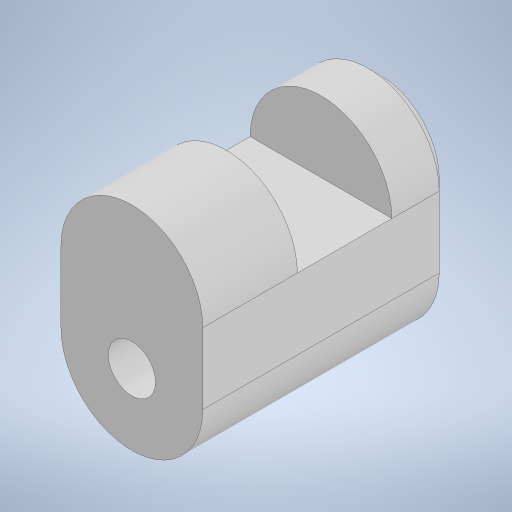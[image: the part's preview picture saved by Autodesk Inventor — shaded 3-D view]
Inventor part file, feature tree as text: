
AUTODESK INVENTOR PART (.ipt)
format: ipt  version: 2024.1 (Build 281209000, 209)  size: 236,544 bytes
history: native  units: mm
features: extrude x4, sketch x4, projected_geometry x3, chamfer x2
ambient origin geometry x8: Origin, YZ Plane, XZ Plane, XY Plane, X Axis, Y Axis, Z Axis, Center Point
bodies: Solid1 (feature_tree)
feature tree (13):
  extrude  "Extrusion1"  Depth=12.0mm
  extrude  "Extrusion2"  Depth=6.0mm
  extrude  "Extrusion3"  Depth=8.0mm TaperAngle=0.0deg
  extrude  "Extrusion4"  Depth=2.0mm TaperAngle=0.0deg
  chamfer  "Chamfer1"  Distance=2.0mm Angle=45.0deg
  chamfer  "Chamfer2"  Distance=2.0mm Angle=45.0deg
  sketch  "Sketch2"  dims[d0=12.0mm d1=4.0mm]
  sketch  "Sketch3"  dims[d2=21.0mm d3=0.0mm d4=6.0mm]
  projected_geometry  "Projected Loop1"
  sketch  "Sketch4"  dims[d5=6.0mm d6=8.0mm d7=0.0mm]
  projected_geometry  "Projected Loop2"
  sketch  "Sketch5"  dims[d8=5.0mm d9=0.0mm d10=8.2mm d11=0.0mm d12=3.0mm d13=2.0mm d14=45.0deg d15=1.0mm d16=2.0mm d17=45.0deg]
  projected_geometry  "Projected Loop3"
